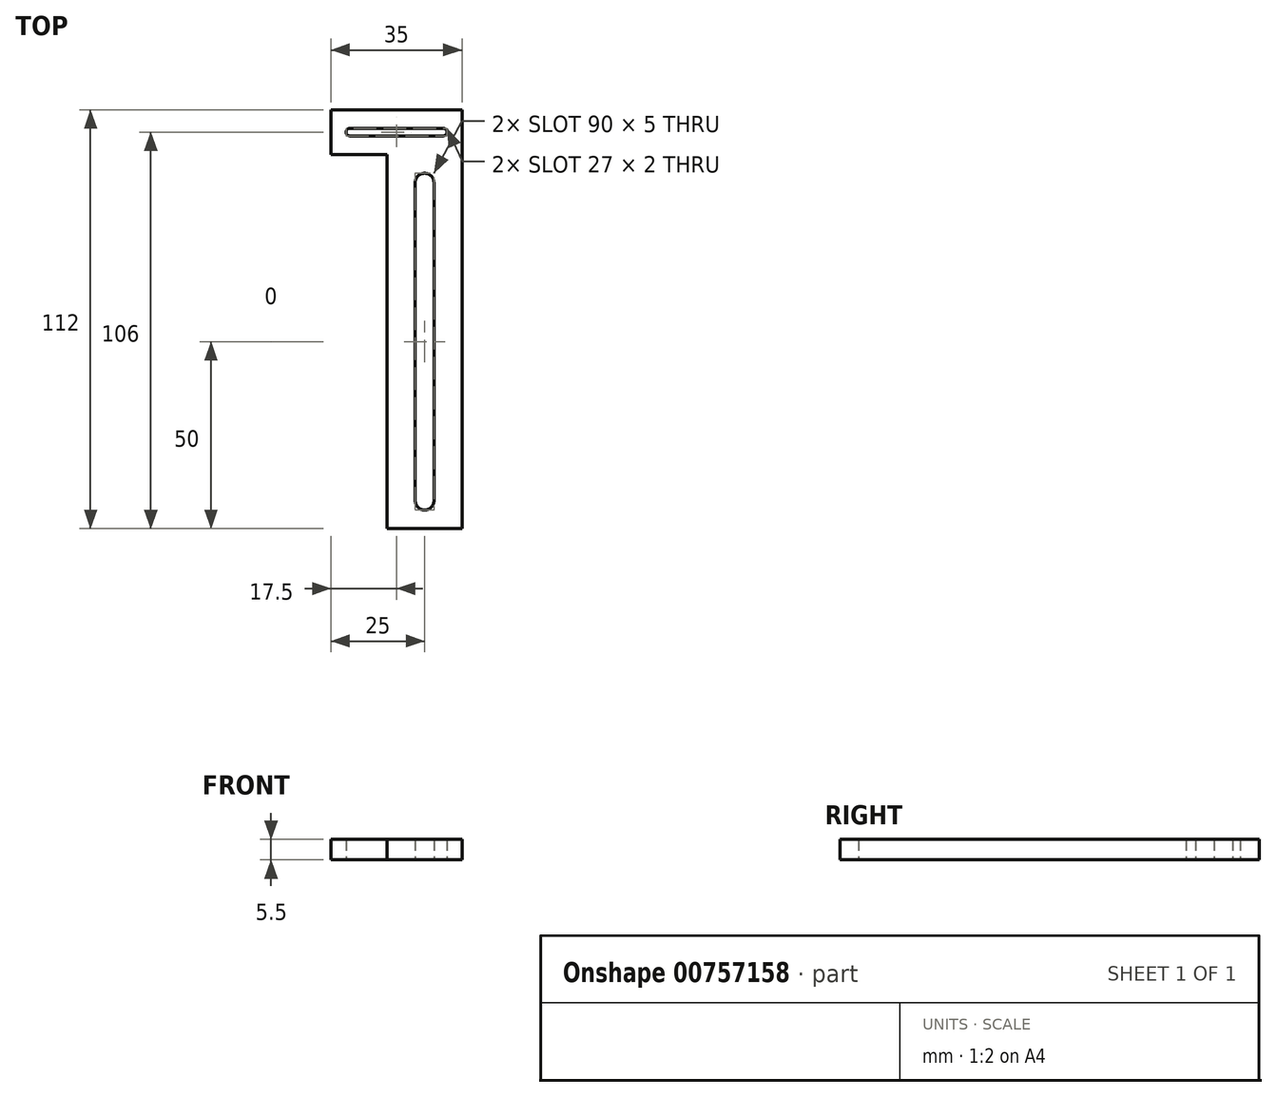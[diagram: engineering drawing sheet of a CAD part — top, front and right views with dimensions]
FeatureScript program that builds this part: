
annotation { "Feature Type Name" : "Feature", "Feature Type Description" : "" }
export const myFeature = defineFeature(function(context is Context, id is Id, definition is map)
    precondition{}
    {
        {
            var Q0;
            Q0=qCreatedBy(makeId("Top.planeOp"),FACE);
            var sketch = newSketch(context, id + "F0", { "sketchPlane" : qUnion([Q0])});
            skLineSegment(sketch, "E0.bottom", {"start": v(0, 0) * mm, "end": v(20, 0) * mm});
            skLineSegment(sketch, "E0.left", {"start": v(0, 0) * mm, "end": v(0, 100) * mm});
            skLineSegment(sketch, "E0.right", {"start": v(20, 0) * mm, "end": v(20, 112) * mm});
            skArc(sketch, "E1", {"start": v(7.5, 7.5) * mm, "mid": v(10, 5) * mm, "end": v(12.5, 7.5) * mm});
            skArc(sketch, "E2", {"start": v(12.5, 92.47) * mm, "mid": v(10.01, 95) * mm, "end": v(7.5, 92.5) * mm});
            skLineSegment(sketch, "E3", {"start": v(-15, 112) * mm, "end": v(-15, 100) * mm});
            skLineSegment(sketch, "E4", {"start": v(-15, 100) * mm, "end": v(0, 100) * mm});
            skLineSegment(sketch, "E5", {"start": v(-15, 106) * mm, "end": v(20, 106) * mm, "construction": true});
            skLineSegment(sketch, "E6", {"start": v(10, 92.5) * mm, "end": v(10, 7.5) * mm, "construction": true});
            skPoint(sketch, "E7", {"position": v(10, 50) * mm});
            skLineSegment(sketch, "E8", {"start": v(0, 100) * mm, "end": v(20, 100) * mm, "construction": true});
            skLineSegment(sketch, "E9", {"start": v(0, 50) * mm, "end": v(10, 50) * mm, "construction": true});
            skLineSegment(sketch, "E10", {"start": v(7.5, 92.5) * mm, "end": v(7.5, 7.5) * mm});
            skLineSegment(sketch, "E11", {"start": v(12.5, 92.47) * mm, "end": v(12.5, 7.5) * mm});
            skLineSegment(sketch, "E12", {"start": v(-15, 112) * mm, "end": v(20, 112) * mm});
            skArc(sketch, "E13", {"start": v(15, 105) * mm, "mid": v(16, 106) * mm, "end": v(15, 107) * mm});
            skLineSegment(sketch, "E14", {"start": v(2.5, 112) * mm, "end": v(2.5, 100) * mm, "construction": true});
            skArc(sketch, "E15.MirrorC", {"start": v(-10, 105) * mm, "mid": v(-11, 106) * mm, "end": v(-10, 107) * mm});
            skLineSegment(sketch, "E16", {"start": v(-10, 107) * mm, "end": v(15, 107) * mm});
            skLineSegment(sketch, "E17", {"start": v(-10, 105) * mm, "end": v(15, 105) * mm});
            skSolve(sketch);
        }
        {
            var Q0;
            Q0=makeQuery(id+"F0.imprint","IMPRINT",FACE,{"disambiguationData":[TD([[makeQuery(id+"F0.imprint","IMPRINT",EDGE,{"derivedFrom":sQuery(id+"F0.wireOp",EDGE,"E0.bottom")}),1.0]])]});
            extrude(context, id + "F1", {"entities" : qUnion([Q0]), "depth" : 5.5 * mm, "offsetDistance" : 25 * mm});
        }
    });
